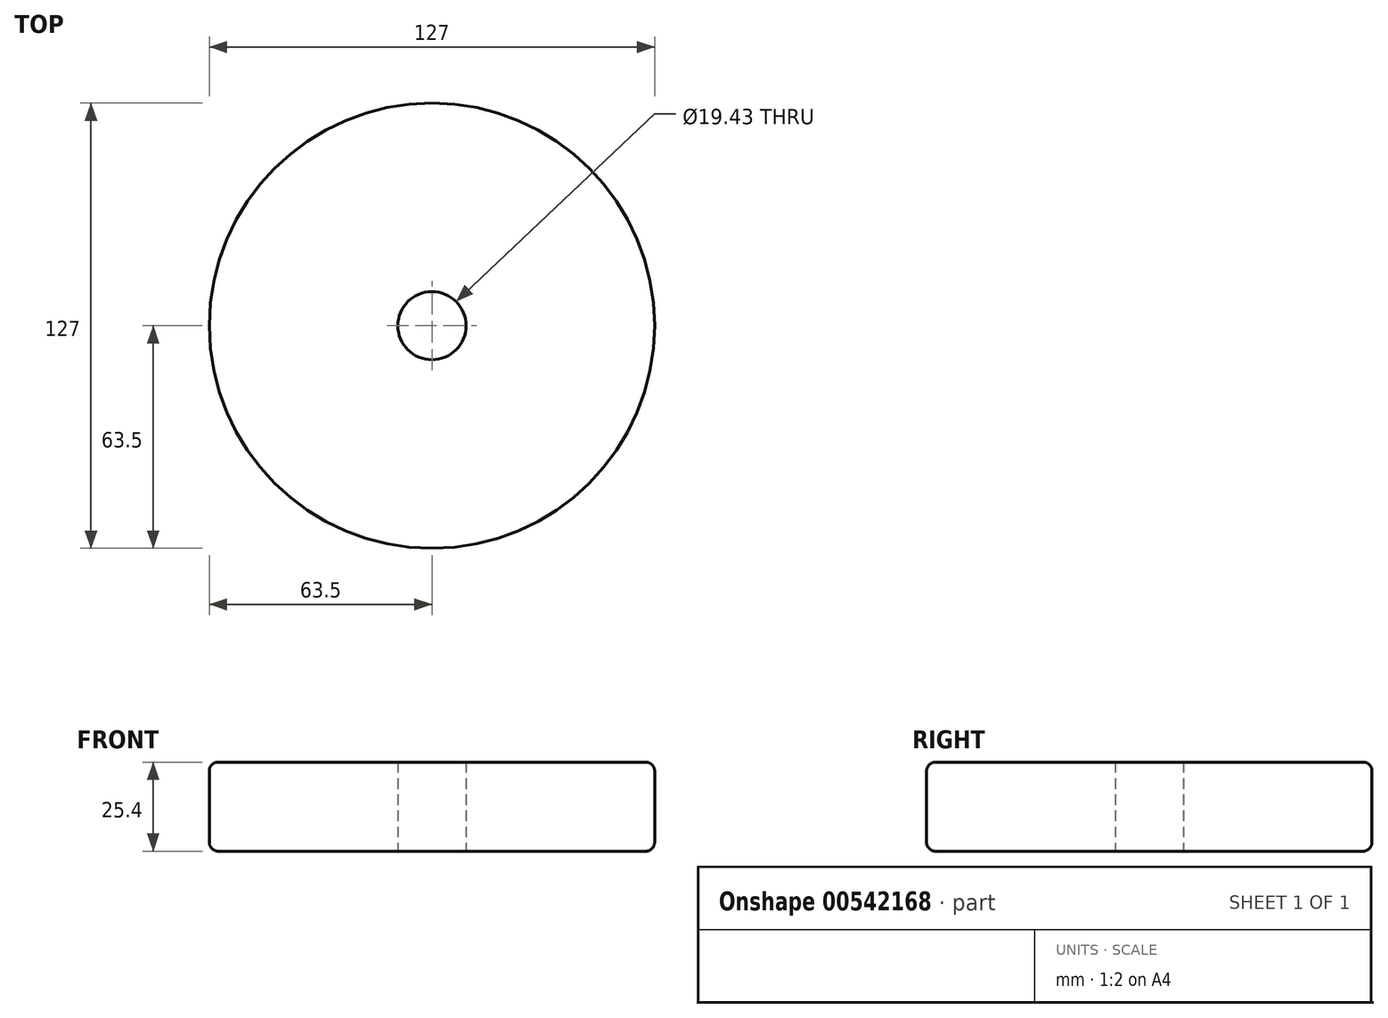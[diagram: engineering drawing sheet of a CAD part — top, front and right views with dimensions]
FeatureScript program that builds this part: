
annotation { "Feature Type Name" : "Feature", "Feature Type Description" : "" }
export const myFeature = defineFeature(function(context is Context, id is Id, definition is map)
    precondition{}
    {
        {
            var Q0;
            Q0=qCreatedBy(makeId("Top.planeOp"),FACE);
            var sketch = newSketch(context, id + "F0", { "sketchPlane" : qUnion([Q0])});
            skCircle(sketch, "E0", {"center": v(0, 0) * mm, "radius": 63.5 * mm});
            skCircle(sketch, "E1", {"center": v(0, 0) * mm, "radius": 4.13 * mm});
            skSolve(sketch);
        }
        {
            var Q0;
            Q0=makeQuery(id+"F0.imprint","IMPRINT",FACE,{"disambiguationData":[TD([[makeQuery(id+"F0.imprint","IMPRINT",EDGE,{"derivedFrom":sQuery(id+"F0.wireOp",EDGE,"E0")}),1.0]])]});
            extrude(context, id + "F1", {"entities" : qUnion([Q0]), "depth" : 25.4 * mm, "offsetDistance" : 25.4 * mm});
        }
        {
            var Q0;
            Q0=makeQuery(id+"F1.opExtrude","CAP_EDGE",EDGE,{"disambiguationData":[OSD([sQuery(id+"F0.wireOp",EDGE,"E0")])],"isStart":false});
            var Q1;
            Q1=makeQuery(id+"F1.opExtrude","CAP_EDGE",EDGE,{"disambiguationData":[OSD([sQuery(id+"F0.wireOp",EDGE,"E0")])],"isStart":true});
            fillet(context, id + "F2", {"entities" : qUnion([Q0, Q1]), "radius" : 2.54 * mm, "tangentPropagation" : true, "allowEdgeOverflow" : false});
        }
        {
            var Q0;
            Q0=qCreatedBy(makeId("Top.planeOp"),FACE);
            var sketch = newSketch(context, id + "F3", { "sketchPlane" : qUnion([Q0])});
            skCircle(sketch, "E2", {"center": v(0, 0) * mm, "radius": 9.72 * mm});
            skSolve(sketch);
        }
        {
            var Q0;
            Q0 = qSketchRegion(id + "F3", true);
            extrude(context, id + "F4", {"entities" : qUnion([Q0]), "operationType" : NewBodyOperationType.REMOVE, "endBound" : BoundingType.SYMMETRIC, "depth" : 812.8 * mm, "offsetDistance" : 25.4 * mm});
        }
    });
